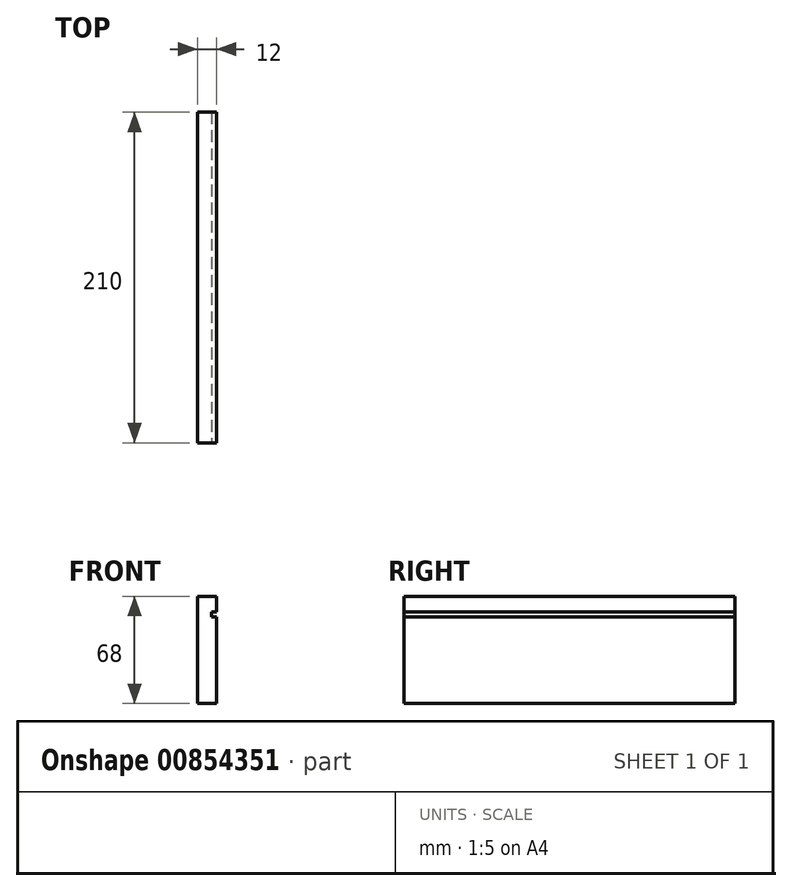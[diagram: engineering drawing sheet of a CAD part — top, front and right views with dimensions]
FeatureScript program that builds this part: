
annotation { "Feature Type Name" : "Feature", "Feature Type Description" : "" }
export const myFeature = defineFeature(function(context is Context, id is Id, definition is map)
    precondition{}
    {
        {
            var Q0;
            Q0=qCreatedBy(makeId("Right.planeOp"),FACE);
            var sketch = newSketch(context, id + "F0", { "sketchPlane" : qUnion([Q0])});
            skLineSegment(sketch, "E0.bottom", {"start": v(-105, 34) * mm, "end": v(105, 34) * mm});
            skLineSegment(sketch, "E0.top", {"start": v(-105, -34) * mm, "end": v(105, -34) * mm});
            skLineSegment(sketch, "E0.left", {"start": v(-105, 34) * mm, "end": v(-105, -34) * mm});
            skLineSegment(sketch, "E0.right", {"start": v(105, 34) * mm, "end": v(105, -34) * mm});
            skPoint(sketch, "E0.middle", {"position": v(0, 0) * mm});
            skSolve(sketch);
        }
        {
            var Q0;
            Q0 = qSketchRegion(id + "F0", true);
            extrude(context, id + "F1", {"entities" : qUnion([Q0]), "depth" : 12 * mm, "offsetDistance" : 25.4 * mm});
        }
        {
            var Q0;
            Q0=makeQuery(id+"F1.opExtrude","SWEPT_FACE",FACE,{"disambiguationData":[OSD([sQuery(id+"F0.wireOp",EDGE,"E0.left")])]});
            var sketch = newSketch(context, id + "F2", { "sketchPlane" : qUnion([Q0])});
            skLineSegment(sketch, "E1.bottom", {"start": v(0, 21) * mm, "end": v(3, 21) * mm});
            skLineSegment(sketch, "E1.top", {"start": v(0, 24) * mm, "end": v(3, 24) * mm});
            skLineSegment(sketch, "E1.left", {"start": v(0, 21) * mm, "end": v(0, 24) * mm});
            skLineSegment(sketch, "E1.right", {"start": v(3, 21) * mm, "end": v(3, 24) * mm});
            skSolve(sketch);
        }
        {
            var Q0;
            Q0 = qSketchRegion(id + "F2", true);
            extrude(context, id + "F3", {"entities" : qUnion([Q0]), "operationType" : NewBodyOperationType.REMOVE, "oppositeDirection" : true, "depth" : 222000 * mm, "offsetDistance" : 25.4 * mm});
        }
        {
            var Q0;
            Q0=makeQuery(id+"F1.opExtrude","SWEPT_FACE",FACE,{"disambiguationData":[OSD([sQuery(id+"F0.wireOp",EDGE,"E0.left")])]});
            var sketch = newSketch(context, id + "F4", { "sketchPlane" : qUnion([Q0])});
            skLineSegment(sketch, "E2.bottom", {"start": v(3, 21) * mm, "end": v(0, 21) * mm});
            skLineSegment(sketch, "E2.top", {"start": v(3, 24) * mm, "end": v(0, 24) * mm});
            skLineSegment(sketch, "E2.left", {"start": v(3, 21) * mm, "end": v(3, 24) * mm});
            skLineSegment(sketch, "E2.right", {"start": v(0, 21) * mm, "end": v(0, 24) * mm});
            skSolve(sketch);
        }
        {
            var Q0;
            Q0=makeQuery(id+"F4.imprint","IMPRINT",FACE,{"disambiguationData":[TD([[makeQuery(id+"F4.imprint","IMPRINT",EDGE,{"derivedFrom":sQuery(id+"F4.wireOp",EDGE,"E2.bottom")}),1.0]])]});
            extrude(context, id + "F5", {"entities" : qUnion([Q0]), "operationType" : NewBodyOperationType.ADD, "depth" : -210 * mm, "offsetDistance" : 25.4 * mm});
        }
        {
            var Q0;
            Q0=makeQuery(id+"F5.boolean.opBoolean","MERGE",FACE,{"derivedFrom":[makeQuery(id+"F1.opExtrude","SWEPT_FACE",FACE,{"disambiguationData":[OSD([sQuery(id+"F0.wireOp",EDGE,"E0.left")])]}),makeQuery(id+"F5.opExtrude","CAP_FACE",FACE,{"disambiguationData":[OSD([sQuery(id+"F4.wireOp",EDGE,"E2.bottom"),sQuery(id+"F4.wireOp",EDGE,"E2.top"),sQuery(id+"F4.wireOp",EDGE,"E2.left"),sQuery(id+"F4.wireOp",EDGE,"E2.right")])],"isStart":true})]});
            var sketch = newSketch(context, id + "F6", { "sketchPlane" : qUnion([Q0])});
            skLineSegment(sketch, "E3.bottom", {"start": v(12, 21) * mm, "end": v(9, 21) * mm});
            skLineSegment(sketch, "E3.top", {"start": v(12, 24) * mm, "end": v(9, 24) * mm});
            skLineSegment(sketch, "E3.left", {"start": v(12, 21) * mm, "end": v(12, 24) * mm});
            skLineSegment(sketch, "E3.right", {"start": v(9, 21) * mm, "end": v(9, 24) * mm});
            skSolve(sketch);
        }
        {
            var Q0;
            Q0 = qSketchRegion(id + "F6", true);
            extrude(context, id + "F7", {"entities" : qUnion([Q0]), "operationType" : NewBodyOperationType.REMOVE, "oppositeDirection" : true, "depth" : 300 * mm, "offsetDistance" : 25.4 * mm});
        }
    });
